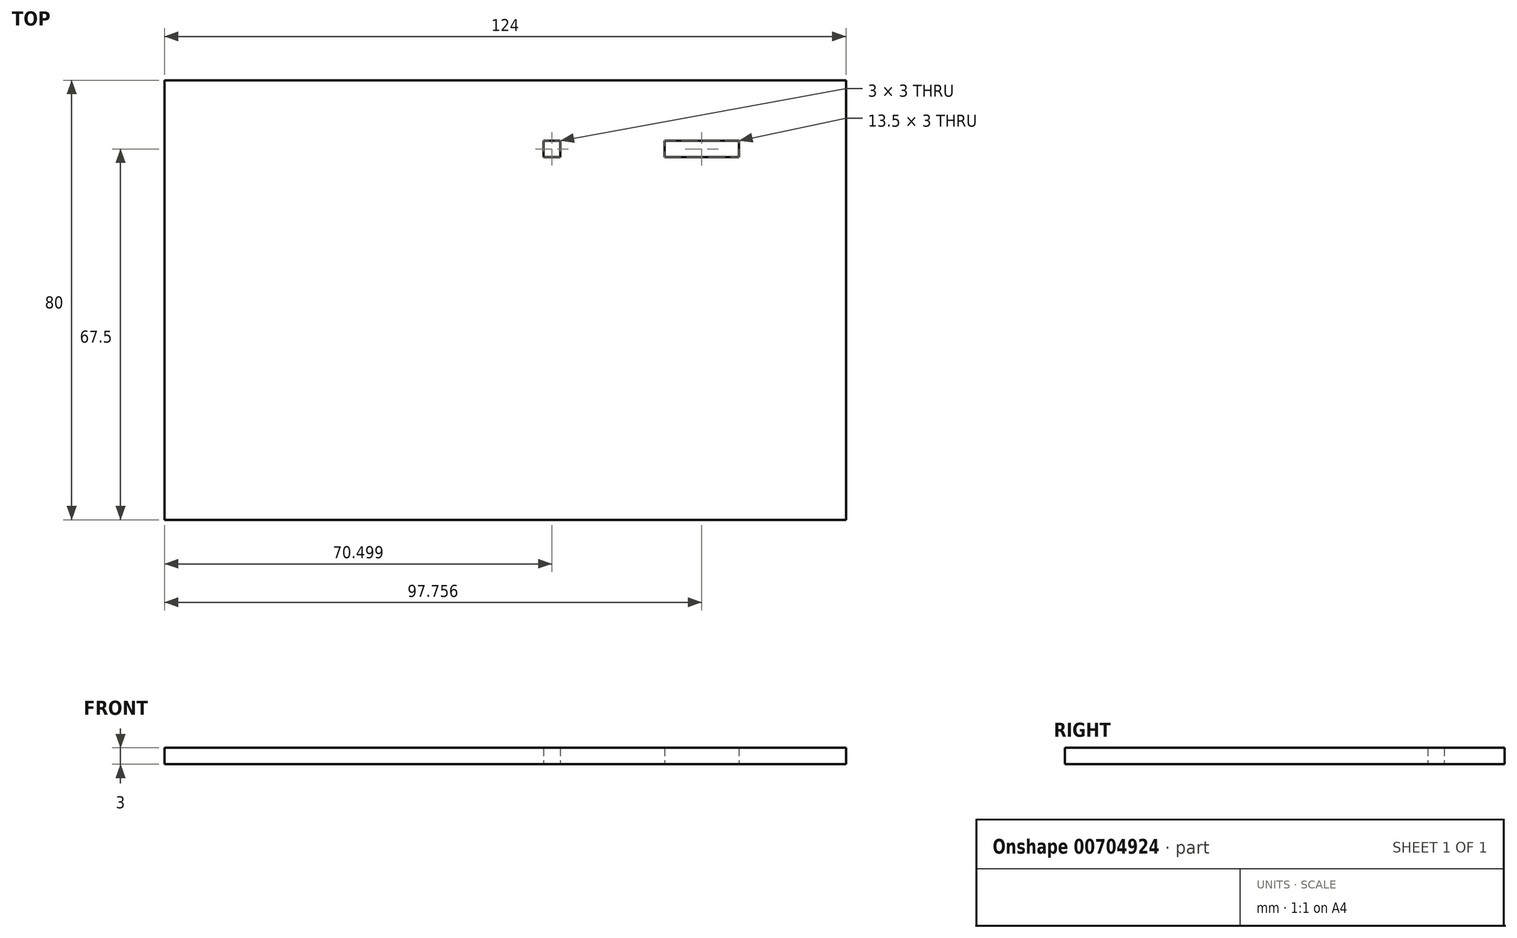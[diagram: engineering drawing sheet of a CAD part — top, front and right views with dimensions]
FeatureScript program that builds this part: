
annotation { "Feature Type Name" : "Feature", "Feature Type Description" : "" }
export const myFeature = defineFeature(function(context is Context, id is Id, definition is map)
    precondition{}
    {
        {
            var Q0;
            Q0=qCreatedBy(makeId("Top.planeOp"),FACE);
            var sketch = newSketch(context, id + "F0", { "sketchPlane" : qUnion([Q0])});
            skLineSegment(sketch, "E0.bottom", {"start": v(-68.04, 70) * mm, "end": v(55.96, 70) * mm});
            skLineSegment(sketch, "E0.top", {"start": v(-68.04, -10) * mm, "end": v(55.96, -10) * mm});
            skLineSegment(sketch, "E0.left", {"start": v(-68.04, 70) * mm, "end": v(-68.04, -10) * mm});
            skLineSegment(sketch, "E0.right", {"start": v(55.96, 70) * mm, "end": v(55.96, -10) * mm});
            skLineSegment(sketch, "E1.MirrorCS", {"start": v(36.47, 56) * mm, "end": v(36.47, 59) * mm});
            skLineSegment(sketch, "E2.MirrorCS", {"start": v(22.97, 56) * mm, "end": v(22.97, 59) * mm});
            skLineSegment(sketch, "E3.MirrorCS", {"start": v(22.97, 56) * mm, "end": v(36.47, 56) * mm});
            skLineSegment(sketch, "E4", {"start": v(36.47, 59) * mm, "end": v(22.97, 59) * mm});
            skLineSegment(sketch, "E5", {"start": v(3.96, 56) * mm, "end": v(0.96, 56) * mm});
            skLineSegment(sketch, "E6", {"start": v(0.96, 56) * mm, "end": v(0.96, 59) * mm});
            skLineSegment(sketch, "E7", {"start": v(0.96, 59) * mm, "end": v(3.96, 59) * mm});
            skLineSegment(sketch, "E8", {"start": v(3.96, 59) * mm, "end": v(3.96, 56) * mm});
            skSolve(sketch);
        }
        {
            var Q0;
            Q0=makeQuery(id+"F0.imprint","IMPRINT",FACE,{"disambiguationData":[TD([[makeQuery(id+"F0.imprint","IMPRINT",EDGE,{"derivedFrom":sQuery(id+"F0.wireOp",EDGE,"UEqrDGLH-FFpF-oJ1Q-Opp3-dnx0jUD92dck")}),1.0]])]});
            var Q1;
            Q1=makeQuery(id+"F0.imprint","IMPRINT",FACE,{"disambiguationData":[TD([[makeQuery(id+"F0.imprint","IMPRINT",EDGE,{"derivedFrom":sQuery(id+"F0.wireOp",EDGE,"E0.bottom")}),-1.0]])]});
            extrude(context, id + "F1", {"entities" : qUnion([Q0, Q1]), "depth" : 3 * mm, "offsetDistance" : 25 * mm});
        }
    });
